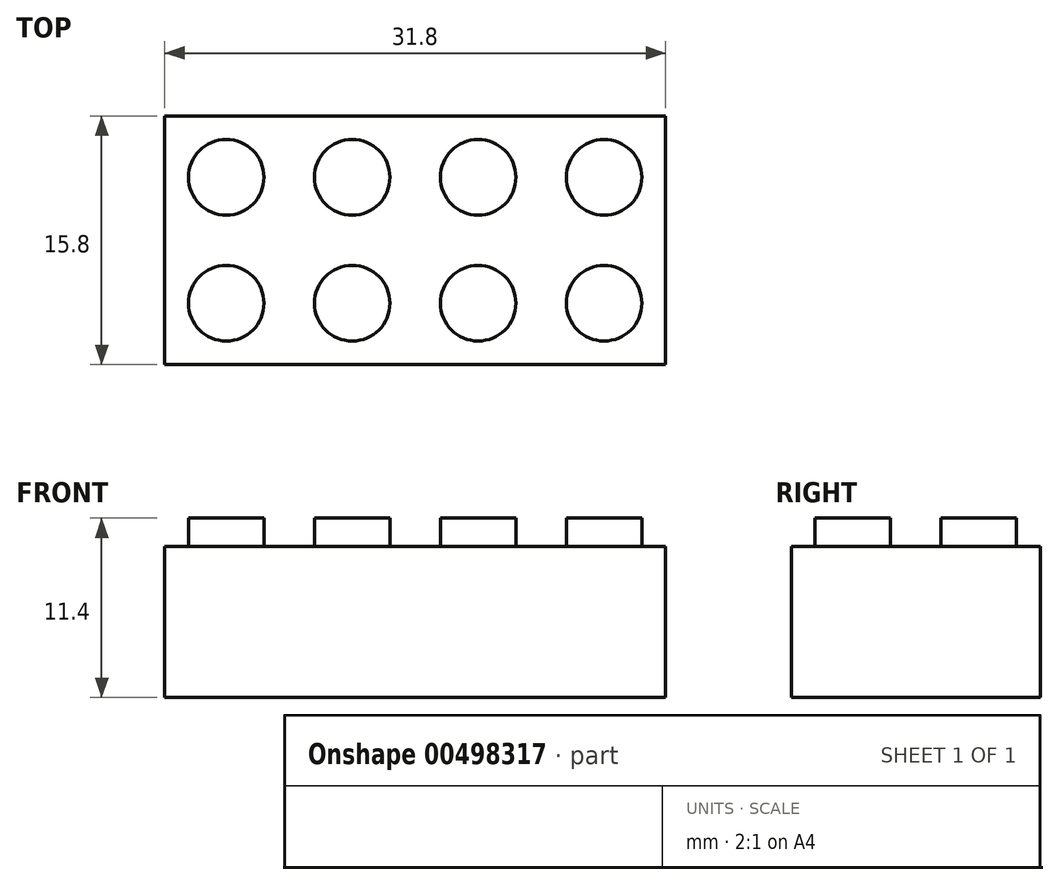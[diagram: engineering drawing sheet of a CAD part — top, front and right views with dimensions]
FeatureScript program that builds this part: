
annotation { "Feature Type Name" : "Feature", "Feature Type Description" : "" }
export const myFeature = defineFeature(function(context is Context, id is Id, definition is map)
    precondition{}
    {
        {
            var Q0;
            Q0=qCreatedBy(makeId("Top.planeOp"),FACE);
            var sketch = newSketch(context, id + "F0", { "sketchPlane" : qUnion([Q0])});
            skLineSegment(sketch, "E0.bottom", {"start": v(-47.85, 42.78) * mm, "end": v(-16.05, 42.78) * mm});
            skLineSegment(sketch, "E0.top", {"start": v(-47.85, 26.98) * mm, "end": v(-16.05, 26.98) * mm});
            skLineSegment(sketch, "E0.left", {"start": v(-47.85, 42.78) * mm, "end": v(-47.85, 26.98) * mm});
            skLineSegment(sketch, "E0.right", {"start": v(-16.05, 42.78) * mm, "end": v(-16.05, 26.98) * mm});
            skSolve(sketch);
        }
        {
            var Q0;
            Q0=makeQuery(id+"F0.imprint","IMPRINT",FACE,{"disambiguationData":[TD([[makeQuery(id+"F0.imprint","IMPRINT",EDGE,{"derivedFrom":sQuery(id+"F0.wireOp",EDGE,"E0.bottom")}),-1.0]])]});
            extrude(context, id + "F1", {"entities" : qUnion([Q0]), "depth" : 9.6 * mm});
        }
        {
            var Q0;
            Q0=makeQuery(id+"F1.opExtrude","CAP_FACE",FACE,{"disambiguationData":[OSD([sQuery(id+"F0.wireOp",EDGE,"E0.bottom"),sQuery(id+"F0.wireOp",EDGE,"E0.top"),sQuery(id+"F0.wireOp",EDGE,"E0.left"),sQuery(id+"F0.wireOp",EDGE,"E0.right")])],"isStart":false});
            var sketch = newSketch(context, id + "F2", { "sketchPlane" : qUnion([Q0])});
            skCircle(sketch, "E1", {"center": v(-43.95, 38.88) * mm, "radius": 2.4 * mm});
            skCircle(sketch, "E2.0.1.0", {"center": v(-43.95, 30.88) * mm, "radius": 2.4 * mm});
            skCircle(sketch, "E2.1.0.0", {"center": v(-35.95, 38.88) * mm, "radius": 2.4 * mm});
            skCircle(sketch, "E2.1.1.0", {"center": v(-35.95, 30.88) * mm, "radius": 2.4 * mm});
            skCircle(sketch, "E2.2.0.0", {"center": v(-27.95, 38.88) * mm, "radius": 2.4 * mm});
            skCircle(sketch, "E2.2.1.0", {"center": v(-27.95, 30.88) * mm, "radius": 2.4 * mm});
            skCircle(sketch, "E2.3.0.0", {"center": v(-19.95, 38.88) * mm, "radius": 2.4 * mm});
            skCircle(sketch, "E2.3.1.0", {"center": v(-19.95, 30.88) * mm, "radius": 2.4 * mm});
            skLineSegment(sketch, "E2.direction1", {"start": v(-43.95, 38.88) * mm, "end": v(-35.95, 38.88) * mm, "construction": true});
            skLineSegment(sketch, "E2.direction2", {"start": v(-43.95, 38.88) * mm, "end": v(-43.95, 30.88) * mm, "construction": true});
            skSolve(sketch);
        }
        {
            var Q0;
            Q0 = qSketchRegion(id + "F2", true);
            extrude(context, id + "F3", {"entities" : qUnion([Q0]), "operationType" : NewBodyOperationType.ADD, "depth" : 1.8 * mm});
        }
    });
